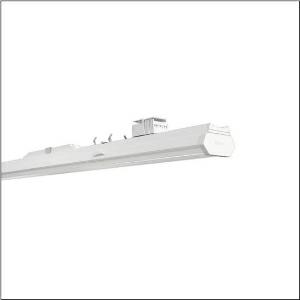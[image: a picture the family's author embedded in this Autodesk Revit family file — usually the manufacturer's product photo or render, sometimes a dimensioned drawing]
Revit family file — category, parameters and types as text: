
# Revit family: licross_r__21_protected_mo_52tp12dn4a5g3s4_4701
name_source: partatom
category: Lighting Fixtures
units: mm (PartAtom-declared; Revit-internal decimal feet)

## family parameters
Cut with Voids When Loaded = No
Host = Face
Light Source = No
Part Type = Normal
Room Calculation Point = No
Round Connector Dimension = Use Diameter
Shared = No

## types (1)
- --- (1 x LED, 940 lm, 6.8 W, 4000K)
    Apparent Load = 7 VA
    CIE Flux Codes = 73 92 98 99 100
    Color Rendering = 80
    Color Temperature = 4000K
    Default Elevation = 1800 mm
    Description = Licross® 21 Protected MO, luminaire insert, of sheet steel, galvanised, coil coated, white, length: 1.500mm, width: 90mm, height: 103mm, LED rated luminous flux: 10.700lm, light colour: 840, control gear: DALI 2, with plug, 6-pole, with phase selection, for trunking rail, 9 or 11-core, mains connection: 220..240V, AC, 50/60Hz, rated input power: 66W, for trunking rail, 9-/11-core, halogen-free wiring, for emergency light function, converter,control gear: single battery element, battery: LiFePO4, 9Ah, primary light control with lens, of plastic, primary optical cover: cover, of PMMA, light emission: direct distribution, primary light characteristic: symmetric, protection rating (complete): IP64, insulation class (complete): insulation class I (protective earthing), certification: CE, UKCA, protection symbol: D if used in an environment with conductive dust loads with corresponding accessories, impact resistance: IK06, permissible ambient temperature for indoor applications: +5..+35°C, standard: EN 60598-2-22, LABS conformity tested according to VDMA 24364:2018-05, reducing of maximum allowable ambient temperature of 5°C with ceiling mounting, corresponds to IFS (International Featured Standards) requirements for safety and quality in the food industry, packaging unit: 1 piece
    Height = 92 mm
    Lamp = 1 x LED
    Lamp Light Flux = 940 lm
    Lamp Power = 6.8 W
    Lamp count = 1
    Length = 1500 mm
    Luminous efficacy = 138 lm/W
    Manufacturer = Siteco
    ModVariant = No
    Model = 52TP12DN4A5G3S4
    Mounting Place = Ceiling
    Mounting Type = Pendant
    Number of Poles = 1
    OnlyDefault = Yes
    Power Factor = 1
    Product Name = Licross® 21 Protected MO
    Product group = luminaire insert
    ProductGroupID = 902
    Protection Class = Protection class I
    Protection Degree = IP 64
    RLX_Detail_Level = 1
    RLX_Emergency_Light_Flux = 0 lm
    RLX_Emergency_Type = 0
    RLX_Emergency_Type_DB = No
    RlxData = <blob elided: 24777 chars, md5=eddccd1f>
    Socket = socket
    Standby Power = 0 W
    System Light Flux = 940 lm
    System Power = 7 W
    Type Comments = : emergency light operation: 3 h
    Type Image = l_1256148.jpg
    URL = http://relux.com
    VarID = @adj_110926
    Voltage = 0 V
    Weight = 0.00 kg
    Width = 88 mm

## geometry (parser evidence)
native form markers: Blend x4, Sweep x9
no freeform markers — native parametric forms only
